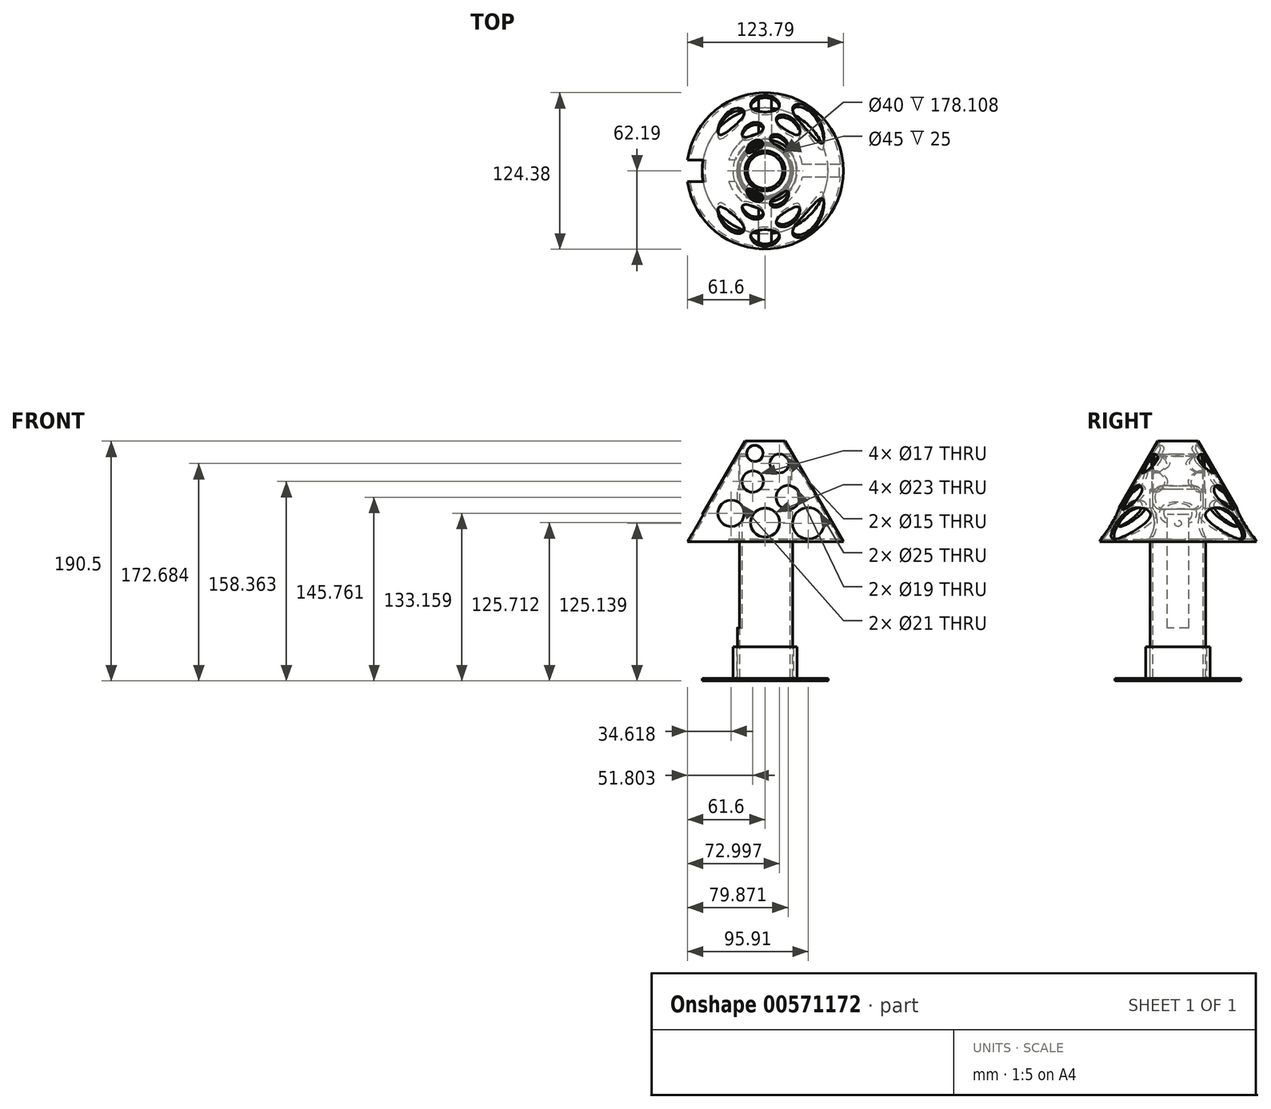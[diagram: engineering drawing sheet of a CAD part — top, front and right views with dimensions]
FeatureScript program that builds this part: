
annotation { "Feature Type Name" : "Feature", "Feature Type Description" : "" }
export const myFeature = defineFeature(function(context is Context, id is Id, definition is map)
    precondition{}
    {
        {
            var Q0;
            Q0=qCreatedBy(makeId("Front.planeOp"),FACE);
            var sketch = newSketch(context, id + "F0", { "sketchPlane" : qUnion([Q0])});
            skLineSegment(sketch, "E0", {"start": v(0, 172.83) * mm, "end": v(0, -197.58) * mm, "construction": true});
            skLineSegment(sketch, "E1", {"start": v(-208.43, 0) * mm, "end": v(198.15, 0) * mm, "construction": true});
            skLineSegment(sketch, "E2", {"start": v(20, 0) * mm, "end": v(20, 150) * mm});
            skLineSegment(sketch, "E3", {"start": v(20, 150) * mm, "end": v(22, 150) * mm});
            skLineSegment(sketch, "E4", {"start": v(22, 150) * mm, "end": v(22, 0) * mm});
            skLineSegment(sketch, "E5", {"start": v(22, 0) * mm, "end": v(20, 0) * mm});
            skSolve(sketch);
        }
        {
            var Q0;
            Q0 = qSketchRegion(id + "F0", true);
            var Q1;
            Q1=sQuery(id+"F0.wireOp",EDGE,"E0");
            revolve(context, id + "F1", {"entities" : qUnion([Q0]), "axis" : qUnion([Q1]), "revolveType" : RevolveType.FULL});
        }
        {
            var Q0;
            Q0=qCreatedBy(makeId("Front.planeOp"),FACE);
            var sketch = newSketch(context, id + "F2", { "sketchPlane" : qUnion([Q0])});
            skPoint(sketch, "E6", {"position": v(16, 188.5) * mm});
            skPoint(sketch, "E7", {"position": v(22, 108.5) * mm});
            skLineSegment(sketch, "E8", {"start": v(16, 188.5) * mm, "end": v(62.19, 108.5) * mm});
            skLineSegment(sketch, "E9", {"start": v(62.19, 108.5) * mm, "end": v(25, 108.5) * mm});
            skLineSegment(sketch, "E10", {"start": v(16, 188.5) * mm, "end": v(14, 188.5) * mm});
            skLineSegment(sketch, "E11", {"start": v(14, 188.5) * mm, "end": v(59.03, 110.5) * mm});
            skLineSegment(sketch, "E12", {"start": v(59.03, 110.5) * mm, "end": v(25, 110.5) * mm});
            skPoint(sketch, "E13", {"position": v(25, 110.5) * mm});
            skLineSegment(sketch, "E14", {"start": v(25, 110.5) * mm, "end": v(25, 108.5) * mm});
            skPoint(sketch, "E15.start.orphan", {"position": v(22, 110.5) * mm});
            skLineSegment(sketch, "E16", {"start": v(0, 193.45) * mm, "end": v(0, -66.14) * mm, "construction": true});
            skSolve(sketch);
        }
        {
            var Q0;
            Q0 = qSketchRegion(id + "F2", true);
            var Q1;
            Q1=sQuery(id+"F2.wireOp",EDGE,"E16");
            revolve(context, id + "F3", {"entities" : qUnion([Q0]), "axis" : qUnion([Q1]), "revolveType" : RevolveType.FULL});
        }
        {
            var Q0;
            Q0=makeQuery(id+"F3.opRevolve","SWEPT_FACE",FACE,{"disambiguationData":[OSD([sQuery(id+"F2.wireOp",EDGE,"E9")])]});
            var sketch = newSketch(context, id + "F4", { "sketchPlane" : qUnion([Q0])});
            skLineSegment(sketch, "E17.bottom", {"start": v(61.99, -5) * mm, "end": v(29.58, -5) * mm});
            skLineSegment(sketch, "E17.top", {"start": v(61.99, 5) * mm, "end": v(29.58, 5) * mm});
            skPoint(sketch, "E17.middle", {"position": v(0, 0) * mm});
            skArc(sketch, "E18.0", {"start": v(61.99, 5) * mm, "mid": v(62.19, 0) * mm, "end": v(61.99, -5) * mm});
            skLineSegment(sketch, "E19.1.0", {"start": v(5, 61.99) * mm, "end": v(5, 29.58) * mm});
            skLineSegment(sketch, "E19.1.1", {"start": v(-5, 61.99) * mm, "end": v(-5, 29.58) * mm});
            skArc(sketch, "E19.1.2", {"start": v(-5, 61.99) * mm, "mid": v(0, 62.19) * mm, "end": v(5, 61.99) * mm});
            skLineSegment(sketch, "E19.3.0", {"start": v(-5, -61.99) * mm, "end": v(-5, -29.58) * mm});
            skLineSegment(sketch, "E19.3.1", {"start": v(5, -61.99) * mm, "end": v(5, -29.58) * mm});
            skArc(sketch, "E19.3.2", {"start": v(5, -61.99) * mm, "mid": v(0, -62.19) * mm, "end": v(-5, -61.99) * mm});
            skLineSegment(sketch, "E20.MirrorCS", {"start": v(-61.99, 5) * mm, "end": v(-29.58, 5) * mm});
            skLineSegment(sketch, "E21.MirrorCS", {"start": v(-61.99, -5) * mm, "end": v(-29.58, -5) * mm});
            skArc(sketch, "E22.MirrorCS", {"start": v(-61.99, 5) * mm, "mid": v(-62.19, 0) * mm, "end": v(-61.99, -5) * mm});
            skPoint(sketch, "E23.orphan", {"position": v(-29.4, 6) * mm});
            skPoint(sketch, "E24.orphan", {"position": v(-29.4, -6) * mm});
            skPoint(sketch, "E25.orphan", {"position": v(-24.5, -5) * mm});
            skPoint(sketch, "E26.orphan", {"position": v(-24.5, 5) * mm});
            skPoint(sketch, "E27.orphan", {"position": v(29.4, -6) * mm});
            skPoint(sketch, "E28.orphan", {"position": v(29.4, 6) * mm});
            skPoint(sketch, "E29.0.end.orphan", {"position": v(24.5, 5) * mm});
            skPoint(sketch, "E29.0.start.orphan", {"position": v(24.5, -5) * mm});
            skCircle(sketch, "E30", {"center": v(0, 0) * mm, "radius": 30 * mm});
            skSolve(sketch);
        }
        {
            var Q0;
            {var subQ0=sQuery(id+"F4.wireOp",EDGE,"E17.top");Q0=makeQuery(id+"F4.imprint","IMPRINT",FACE,{"disambiguationData":[TD([[makeQuery(id+"F4.imprint","IMPRINT",EDGE,{"derivedFrom":subQ0}),-1.0]])]});}
            var Q1;
            {var subQ0=sQuery(id+"F4.wireOp",EDGE,"E19.1.1");Q1=makeQuery(id+"F4.imprint","IMPRINT",FACE,{"disambiguationData":[TD([[makeQuery(id+"F4.imprint","IMPRINT",EDGE,{"derivedFrom":subQ0}),-1.0]])]});}
            var Q2;
            {var subQ0=sQuery(id+"F4.wireOp",EDGE,"E19.3.0");Q2=makeQuery(id+"F4.imprint","IMPRINT",FACE,{"disambiguationData":[TD([[makeQuery(id+"F4.imprint","IMPRINT",EDGE,{"derivedFrom":subQ0}),1.0]])]});}
            var Q3;
            {var subQ0=sQuery(id+"F4.wireOp",EDGE,"E17.bottom");Q3=makeQuery(id+"F4.imprint","IMPRINT",FACE,{"disambiguationData":[TD([[makeQuery(id+"F4.imprint","IMPRINT",EDGE,{"derivedFrom":subQ0}),1.0]])]});}
            var Q4;
            Q4=makeQuery(id+"F3.opRevolve","SWEPT_FACE",FACE,{"disambiguationData":[OSD([sQuery(id+"F2.wireOp",EDGE,"E11")])]});
            extrude(context, id + "F5", {"entities" : qUnion([Q0, Q1, Q2, Q3]), "operationType" : NewBodyOperationType.REMOVE, "endBound" : BoundingType.UP_TO_SURFACE, "oppositeDirection" : true, "depth" : 2 * mm, "endBoundEntityFace" : qUnion([Q4]), "offsetDistance" : 25 * mm});
        }
        {
            var Q0;
            Q0=makeQuery(id+"F1.opRevolve","SWEPT_FACE",FACE,{"disambiguationData":[OSD([sQuery(id+"F0.wireOp",EDGE,"E3")])]});
            var sketch = newSketch(context, id + "F6", { "sketchPlane" : qUnion([Q0])});
            skCircle(sketch, "E31", {"center": v(0, 0) * mm, "radius": 21 * mm});
            skCircle(sketch, "E32.0", {"center": v(0, 0) * mm, "radius": 20 * mm});
            skSolve(sketch);
        }
        {
            var Q0;
            Q0 = qSketchRegion(id + "F6", true);
            var Q1;
            Q1=makeQuery(id+"F3.opRevolve","SWEPT_BODY",BODY,{"disambiguationData":[OSD([sQuery(id+"F2.wireOp",EDGE,"E8"),sQuery(id+"F2.wireOp",EDGE,"E9"),sQuery(id+"F2.wireOp",EDGE,"E10"),sQuery(id+"F2.wireOp",EDGE,"E11"),sQuery(id+"F2.wireOp",EDGE,"E12"),sQuery(id+"F2.wireOp",EDGE,"E14")])]});
            extrude(context, id + "F7", {"entities" : qUnion([Q0]), "operationType" : NewBodyOperationType.ADD, "endBound" : BoundingType.UP_TO_BODY, "depth" : 25 * mm, "endBoundEntityBody" : qUnion([Q1]), "offsetDistance" : 25 * mm});
        }
        {
            var Q0;
            Q0=qCreatedBy(makeId("Top.planeOp"),FACE);
            var sketch = newSketch(context, id + "F8", { "sketchPlane" : qUnion([Q0])});
            skCircle(sketch, "E33", {"center": v(0, 0) * mm, "radius": 22.5 * mm});
            skCircle(sketch, "E34.0", {"center": v(0, 0) * mm, "radius": 25.5 * mm});
            skSolve(sketch);
        }
        {
            var Q0;
            Q0 = qSketchRegion(id + "F8", true);
            extrude(context, id + "F9", {"entities" : qUnion([Q0]), "depth" : 25 * mm, "offsetDistance" : 25 * mm});
        }
        {
            var Q0;
            Q0=makeQuery(id+"F9.opExtrude","CAP_FACE",FACE,{"disambiguationData":[OSD([sQuery(id+"F8.wireOp",EDGE,"E33"),sQuery(id+"F8.wireOp",EDGE,"E34.0")])],"isStart":true});
            var sketch = newSketch(context, id + "F10", { "sketchPlane" : qUnion([Q0])});
            skCircle(sketch, "E35.0", {"center": v(0, 0) * mm, "radius": 50 * mm});
            skSolve(sketch);
        }
        {
            var Q0;
            Q0 = qSketchRegion(id + "F10", true);
            extrude(context, id + "F11", {"entities" : qUnion([Q0]), "operationType" : NewBodyOperationType.ADD, "depth" : 2 * mm, "offsetDistance" : 25 * mm});
        }
        {
            var Q0;
            Q0=qCreatedBy(makeId("Front.planeOp"),FACE);
            var sketch = newSketch(context, id + "F12", { "sketchPlane" : qUnion([Q0])});
            skCircle(sketch, "E36", {"center": v(-8.08, 178.7) * mm, "radius": 6.5 * mm});
            skCircle(sketch, "E37", {"center": v(11.4, 170.68) * mm, "radius": 7.5 * mm});
            skCircle(sketch, "E38", {"center": v(-9.8, 156.36) * mm, "radius": 8.5 * mm});
            skCircle(sketch, "E39", {"center": v(18.27, 143.76) * mm, "radius": 9.5 * mm});
            skCircle(sketch, "E40", {"center": v(-26.98, 131.16) * mm, "radius": 10.5 * mm});
            skCircle(sketch, "E41", {"center": v(0, 123.71) * mm, "radius": 11.5 * mm});
            skCircle(sketch, "E42", {"center": v(34.31, 123.14) * mm, "radius": 12.5 * mm});
            skSolve(sketch);
        }
        {
            var Q0;
            Q0 = qSketchRegion(id + "F12", true);
            extrude(context, id + "F13", {"entities" : qUnion([Q0]), "operationType" : NewBodyOperationType.REMOVE, "endBound" : BoundingType.THROUGH_ALL, "oppositeDirection" : true, "depth" : 25 * mm, "offsetDistance" : 25 * mm, "hasSecondDirection" : true, "secondDirectionBound" : SecondDirectionBoundingType.THROUGH_ALL, "secondDirectionOppositeDirection" : false, "secondDirectionDepth" : 25 * mm});
        }
        {
            var Q0;
            Q0=qCreatedBy(makeId("Right.planeOp"),FACE);
            var sketch = newSketch(context, id + "F14", { "sketchPlane" : qUnion([Q0])});
            skLineSegment(sketch, "E43", {"start": v(0, 0) * mm, "end": v(0, 85) * mm, "construction": true});
            skLineSegment(sketch, "E44.bottom", {"start": v(8.5, 130) * mm, "end": v(-8.5, 130) * mm});
            skLineSegment(sketch, "E44.top", {"start": v(8.5, 40) * mm, "end": v(-8.5, 40) * mm});
            skLineSegment(sketch, "E44.left", {"start": v(8.5, 130) * mm, "end": v(8.5, 40) * mm});
            skLineSegment(sketch, "E44.right", {"start": v(-8.5, 130) * mm, "end": v(-8.5, 40) * mm});
            skPoint(sketch, "E44.middle", {"position": v(0, 85) * mm});
            skSolve(sketch);
        }
        {
            var Q0;
            Q0 = qSketchRegion(id + "F14", true);
            extrude(context, id + "F15", {"entities" : qUnion([Q0]), "operationType" : NewBodyOperationType.REMOVE, "endBound" : BoundingType.THROUGH_ALL, "oppositeDirection" : true, "depth" : 25 * mm, "offsetDistance" : 25 * mm});
        }
    });
